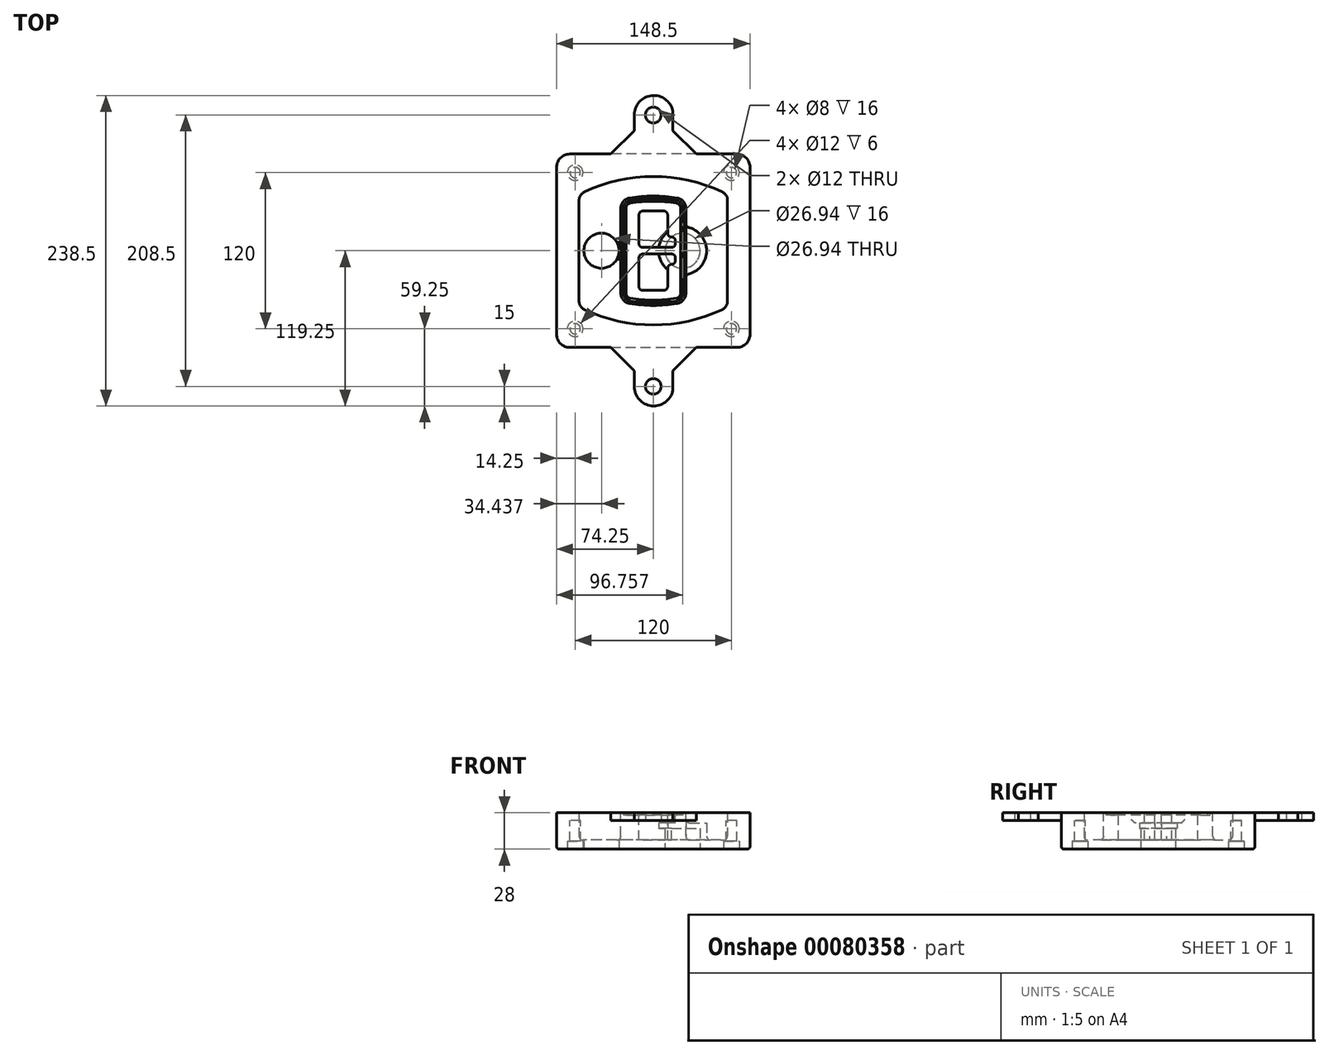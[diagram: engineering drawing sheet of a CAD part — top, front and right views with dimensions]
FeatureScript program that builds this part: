
annotation { "Feature Type Name" : "Feature", "Feature Type Description" : "" }
export const myFeature = defineFeature(function(context is Context, id is Id, definition is map)
    precondition{}
    {
        {
            var Q0;
            Q0=qCreatedBy(makeId("Top.planeOp"),FACE);
            var sketch = newSketch(context, id + "F0", { "sketchPlane" : qUnion([Q0])});
            skPoint(sketch, "E0.rect.middle", {"position": v(0, 0) * mm});
            skLineSegment(sketch, "E1.bottom", {"start": v(-64.25, -74.25) * mm, "end": v(64.25, -74.25) * mm});
            skLineSegment(sketch, "E1.top", {"start": v(-64.25, 74.25) * mm, "end": v(64.25, 74.25) * mm});
            skLineSegment(sketch, "E1.left", {"start": v(-74.25, -64.25) * mm, "end": v(-74.25, 64.25) * mm});
            skLineSegment(sketch, "E1.right", {"start": v(74.25, -64.25) * mm, "end": v(74.25, 64.25) * mm});
            skLineSegment(sketch, "E2", {"start": v(-74.25, 74.25) * mm, "end": v(74.25, -74.25) * mm, "construction": true});
            skLineSegment(sketch, "E3", {"start": v(74.25, 74.25) * mm, "end": v(-74.25, -74.25) * mm, "construction": true});
            skCircle(sketch, "E4", {"center": v(-60, 60) * mm, "radius": 4 * mm});
            skCircle(sketch, "E5", {"center": v(60, 60) * mm, "radius": 4 * mm});
            skCircle(sketch, "E6", {"center": v(60, -60) * mm, "radius": 4 * mm});
            skCircle(sketch, "E7", {"center": v(-60, -60) * mm, "radius": 4 * mm});
            skLineSegment(sketch, "E8", {"start": v(-60, 60) * mm, "end": v(60, 60) * mm, "construction": true});
            skLineSegment(sketch, "E9", {"start": v(60, 60) * mm, "end": v(60, -60) * mm, "construction": true});
            skLineSegment(sketch, "E10", {"start": v(60, -60) * mm, "end": v(-60, -60) * mm, "construction": true});
            skLineSegment(sketch, "E11", {"start": v(-60, -60) * mm, "end": v(-60, 60) * mm, "construction": true});
            skLineSegment(sketch, "E12", {"start": v(-60, 38.83) * mm, "end": v(-60, -38.83) * mm});
            skLineSegment(sketch, "E13", {"start": v(60, 38.83) * mm, "end": v(60, -38.83) * mm});
            skArc(sketch, "E14", {"start": v(54.26, 47.88) * mm, "mid": v(0, 60) * mm, "end": v(-54.26, 47.88) * mm});
            skArc(sketch, "E15", {"start": v(-54.26, -47.88) * mm, "mid": v(0, -60) * mm, "end": v(54.26, -47.88) * mm});
            skLineSegment(sketch, "E16", {"start": v(-60, 0) * mm, "end": v(60, 0) * mm, "construction": true});
            skPoint(sketch, "E17.visualSharp", {"position": v(-60, -45) * mm});
            skArc(sketch, "E17.filletArc", {"start": v(-60, -38.83) * mm, "mid": v(-58.44, -44.2) * mm, "end": v(-54.26, -47.88) * mm});
            skPoint(sketch, "E18.visualSharp", {"position": v(-60, 45) * mm});
            skArc(sketch, "E18.filletArc", {"start": v(-54.26, 47.88) * mm, "mid": v(-58.44, 44.2) * mm, "end": v(-60, 38.83) * mm});
            skPoint(sketch, "E19.visualSharp", {"position": v(60, 45) * mm});
            skArc(sketch, "E19.filletArc", {"start": v(60, 38.83) * mm, "mid": v(58.44, 44.2) * mm, "end": v(54.26, 47.88) * mm});
            skPoint(sketch, "E20.visualSharp", {"position": v(60, -45) * mm});
            skArc(sketch, "E20.filletArc", {"start": v(54.26, -47.88) * mm, "mid": v(58.44, -44.2) * mm, "end": v(60, -38.83) * mm});
            skPoint(sketch, "E21.visualSharp", {"position": v(-74.25, 74.25) * mm});
            skArc(sketch, "E21.filletArc", {"start": v(-64.25, 74.25) * mm, "mid": v(-71.32, 71.32) * mm, "end": v(-74.25, 64.25) * mm});
            skPoint(sketch, "E22.visualSharp", {"position": v(74.25, 74.25) * mm});
            skArc(sketch, "E22.filletArc", {"start": v(74.25, 64.25) * mm, "mid": v(71.32, 71.32) * mm, "end": v(64.25, 74.25) * mm});
            skPoint(sketch, "E23.visualSharp", {"position": v(74.25, -74.25) * mm});
            skArc(sketch, "E23.filletArc", {"start": v(64.25, -74.25) * mm, "mid": v(71.32, -71.32) * mm, "end": v(74.25, -64.25) * mm});
            skPoint(sketch, "E24.visualSharp", {"position": v(-74.25, -74.25) * mm});
            skArc(sketch, "E24.filletArc", {"start": v(-74.25, -64.25) * mm, "mid": v(-71.32, -71.32) * mm, "end": v(-64.25, -74.25) * mm});
            skArc(sketch, "E25.0", {"start": v(57, 38.83) * mm, "mid": v(55.9, 42.58) * mm, "end": v(52.98, 45.17) * mm});
            skLineSegment(sketch, "E25.1", {"start": v(57, 38.83) * mm, "end": v(57, -38.83) * mm});
            skArc(sketch, "E25.2", {"start": v(52.98, -45.17) * mm, "mid": v(55.9, -42.58) * mm, "end": v(57, -38.83) * mm});
            skArc(sketch, "E25.3", {"start": v(-52.98, -45.17) * mm, "mid": v(0, -57) * mm, "end": v(52.98, -45.17) * mm});
            skArc(sketch, "E25.4", {"start": v(-57, -38.83) * mm, "mid": v(-55.9, -42.58) * mm, "end": v(-52.98, -45.17) * mm});
            skArc(sketch, "E25.5", {"start": v(52.98, 45.17) * mm, "mid": v(0, 57) * mm, "end": v(-52.98, 45.17) * mm});
            skLineSegment(sketch, "E25.6", {"start": v(-57, 38.83) * mm, "end": v(-57, -38.83) * mm});
            skArc(sketch, "E25.7", {"start": v(-52.98, 45.17) * mm, "mid": v(-55.9, 42.58) * mm, "end": v(-57, 38.83) * mm});
            skArc(sketch, "E26.0", {"start": v(-55.96, 51.5) * mm, "mid": v(-61.82, 46.33) * mm, "end": v(-64, 38.83) * mm});
            skArc(sketch, "E26.1", {"start": v(55.96, 51.5) * mm, "mid": v(0, 64) * mm, "end": v(-55.96, 51.5) * mm});
            skArc(sketch, "E26.2", {"start": v(64, 38.83) * mm, "mid": v(61.82, 46.33) * mm, "end": v(55.96, 51.5) * mm});
            skLineSegment(sketch, "E26.3", {"start": v(64, 38.83) * mm, "end": v(64, -38.83) * mm});
            skArc(sketch, "E26.4", {"start": v(55.96, -51.5) * mm, "mid": v(61.82, -46.33) * mm, "end": v(64, -38.83) * mm});
            skLineSegment(sketch, "E26.5", {"start": v(-64, 38.83) * mm, "end": v(-64, -38.83) * mm});
            skArc(sketch, "E26.6", {"start": v(-55.96, -51.5) * mm, "mid": v(0, -64) * mm, "end": v(55.96, -51.5) * mm});
            skArc(sketch, "E26.7", {"start": v(-64, -38.83) * mm, "mid": v(-61.82, -46.33) * mm, "end": v(-55.96, -51.5) * mm});
            skSolve(sketch);
        }
        {
            var Q0;
            Q0=makeQuery(id+"F0.imprint","IMPRINT",FACE,{"disambiguationData":[TD([[makeQuery(id+"F0.imprint","IMPRINT",EDGE,{"derivedFrom":sQuery(id+"F0.wireOp",EDGE,"E1.bottom")}),1.0]])]});
            var Q1;
            Q1=makeQuery(id+"F0.imprint","IMPRINT",FACE,{"disambiguationData":[TD([[makeQuery(id+"F0.imprint","IMPRINT",EDGE,{"derivedFrom":sQuery(id+"F0.wireOp",EDGE,"E12")}),1.0]])]});
            var Q2;
            Q2=makeQuery(id+"F0.imprint","IMPRINT",FACE,{"disambiguationData":[TD([[makeQuery(id+"F0.imprint","IMPRINT",EDGE,{"derivedFrom":sQuery(id+"F0.wireOp",EDGE,"E25.0")}),1.0]])]});
            var Q3;
            Q3=makeQuery(id+"F0.imprint","IMPRINT",FACE,{"disambiguationData":[TD([[makeQuery(id+"F0.imprint","IMPRINT",EDGE,{"derivedFrom":sQuery(id+"F0.wireOp",EDGE,"E12")}),-1.0]])]});
            extrude(context, id + "F1", {"entities" : qUnion([Q0, Q1, Q2, Q3]), "oppositeDirection" : true, "depth" : 25 * mm});
        }
        {
            var Q0;
            Q0=makeQuery(id+"F0.imprint","IMPRINT",FACE,{"disambiguationData":[TD([[makeQuery(id+"F0.imprint","IMPRINT",EDGE,{"derivedFrom":sQuery(id+"F0.wireOp",EDGE,"E12")}),1.0]])]});
            extrude(context, id + "F2", {"entities" : qUnion([Q0]), "operationType" : NewBodyOperationType.ADD, "depth" : 3 * mm});
        }
        {
            var Q0;
            Q0=makeQuery(id+"F0.imprint","IMPRINT",FACE,{"disambiguationData":[TD([[makeQuery(id+"F0.imprint","IMPRINT",EDGE,{"derivedFrom":sQuery(id+"F0.wireOp",EDGE,"E25.0")}),1.0]])]});
            extrude(context, id + "F3", {"entities" : qUnion([Q0]), "operationType" : NewBodyOperationType.REMOVE, "oppositeDirection" : true, "depth" : 18 * mm});
        }
        {
            var Q0;
            Q0=makeQuery(id+"F2.opExtrude","CAP_FACE",FACE,{"disambiguationData":[OSD([sQuery(id+"F0.wireOp",EDGE,"E12"),sQuery(id+"F0.wireOp",EDGE,"E13"),sQuery(id+"F0.wireOp",EDGE,"E14"),sQuery(id+"F0.wireOp",EDGE,"E15"),sQuery(id+"F0.wireOp",EDGE,"E17.filletArc"),sQuery(id+"F0.wireOp",EDGE,"E18.filletArc"),sQuery(id+"F0.wireOp",EDGE,"E19.filletArc"),sQuery(id+"F0.wireOp",EDGE,"E20.filletArc"),sQuery(id+"F0.wireOp",EDGE,"E25.0"),sQuery(id+"F0.wireOp",EDGE,"E25.1"),sQuery(id+"F0.wireOp",EDGE,"E25.2"),sQuery(id+"F0.wireOp",EDGE,"E25.3"),sQuery(id+"F0.wireOp",EDGE,"E25.4"),sQuery(id+"F0.wireOp",EDGE,"E25.5"),sQuery(id+"F0.wireOp",EDGE,"E25.6"),sQuery(id+"F0.wireOp",EDGE,"E25.7")])],"isStart":false});
            var sketch = newSketch(context, id + "F4", { "sketchPlane" : qUnion([Q0])});
            skArc(sketch, "E27.0", {"start": v(-18.34, -40.45) * mm, "mid": v(0, -42) * mm, "end": v(18.34, -40.45) * mm});
            skArc(sketch, "E28.0", {"start": v(18.34, 40.45) * mm, "mid": v(0, 42) * mm, "end": v(-18.34, 40.45) * mm});
            skLineSegment(sketch, "E29", {"start": v(-25, 32.57) * mm, "end": v(-25, -32.57) * mm});
            skLineSegment(sketch, "E30", {"start": v(25, 32.57) * mm, "end": v(25, -32.57) * mm});
            skLineSegment(sketch, "E31", {"start": v(-25, 39.1) * mm, "end": v(25, 39.1) * mm, "construction": true});
            skLineSegment(sketch, "E32", {"start": v(-25, -39.1) * mm, "end": v(25, -39.1) * mm, "construction": true});
            skPoint(sketch, "E33.visualSharp", {"position": v(-25, 39.1) * mm});
            skArc(sketch, "E33.filletArc", {"start": v(-18.34, 40.45) * mm, "mid": v(-23.11, 37.73) * mm, "end": v(-25, 32.57) * mm});
            skPoint(sketch, "E34.visualSharp", {"position": v(25, 39.1) * mm});
            skArc(sketch, "E34.filletArc", {"start": v(25, 32.57) * mm, "mid": v(23.11, 37.73) * mm, "end": v(18.34, 40.45) * mm});
            skPoint(sketch, "E35.visualSharp", {"position": v(25, -39.1) * mm});
            skArc(sketch, "E35.filletArc", {"start": v(18.34, -40.45) * mm, "mid": v(23.11, -37.73) * mm, "end": v(25, -32.57) * mm});
            skPoint(sketch, "E36.visualSharp", {"position": v(-25, -39.1) * mm});
            skArc(sketch, "E36.filletArc", {"start": v(-25, -32.57) * mm, "mid": v(-23.11, -37.73) * mm, "end": v(-18.34, -40.45) * mm});
            skArc(sketch, "E37.0", {"start": v(52.98, 45.17) * mm, "mid": v(0, 57) * mm, "end": v(-52.98, 45.17) * mm});
            skArc(sketch, "E37.1", {"start": v(-52.98, 45.17) * mm, "mid": v(-55.9, 42.58) * mm, "end": v(-57, 38.83) * mm});
            skLineSegment(sketch, "E37.2", {"start": v(-57, 38.83) * mm, "end": v(-57, -38.83) * mm});
            skArc(sketch, "E37.3", {"start": v(-57, -38.83) * mm, "mid": v(-55.9, -42.58) * mm, "end": v(-52.98, -45.17) * mm});
            skArc(sketch, "E37.4", {"start": v(-52.98, -45.17) * mm, "mid": v(0, -57) * mm, "end": v(52.98, -45.17) * mm});
            skArc(sketch, "E37.5", {"start": v(52.98, -45.17) * mm, "mid": v(55.9, -42.58) * mm, "end": v(57, -38.83) * mm});
            skLineSegment(sketch, "E37.6", {"start": v(57, 38.83) * mm, "end": v(57, -38.83) * mm});
            skArc(sketch, "E37.7", {"start": v(57, 38.83) * mm, "mid": v(55.9, 42.58) * mm, "end": v(52.98, 45.17) * mm});
            skLineSegment(sketch, "E38.0", {"start": v(23, 32.57) * mm, "end": v(23, -32.57) * mm});
            skArc(sketch, "E38.1", {"start": v(18, -38.48) * mm, "mid": v(21.58, -36.44) * mm, "end": v(23, -32.57) * mm});
            skArc(sketch, "E38.2", {"start": v(-18, -38.48) * mm, "mid": v(0, -40) * mm, "end": v(18, -38.48) * mm});
            skArc(sketch, "E38.3", {"start": v(-23, -32.57) * mm, "mid": v(-21.58, -36.44) * mm, "end": v(-18, -38.48) * mm});
            skLineSegment(sketch, "E38.4", {"start": v(-23, 32.57) * mm, "end": v(-23, -32.57) * mm});
            skArc(sketch, "E38.5", {"start": v(23, 32.57) * mm, "mid": v(21.58, 36.44) * mm, "end": v(18, 38.48) * mm});
            skArc(sketch, "E38.6", {"start": v(-18, 38.48) * mm, "mid": v(-21.58, 36.44) * mm, "end": v(-23, 32.57) * mm});
            skArc(sketch, "E38.7", {"start": v(18, 38.48) * mm, "mid": v(0, 40) * mm, "end": v(-18, 38.48) * mm});
            skArc(sketch, "E39.0", {"start": v(21, 32.57) * mm, "mid": v(20.06, 35.15) * mm, "end": v(17.67, 36.5) * mm});
            skLineSegment(sketch, "E39.1", {"start": v(21, 32.57) * mm, "end": v(21, -32.57) * mm});
            skArc(sketch, "E39.2", {"start": v(17.67, -36.5) * mm, "mid": v(20.06, -35.15) * mm, "end": v(21, -32.57) * mm});
            skArc(sketch, "E39.3", {"start": v(-17.67, -36.5) * mm, "mid": v(0, -38) * mm, "end": v(17.67, -36.5) * mm});
            skArc(sketch, "E39.4", {"start": v(-21, -32.57) * mm, "mid": v(-20.06, -35.15) * mm, "end": v(-17.67, -36.5) * mm});
            skArc(sketch, "E39.5", {"start": v(17.67, 36.5) * mm, "mid": v(0, 38) * mm, "end": v(-17.67, 36.5) * mm});
            skLineSegment(sketch, "E39.6", {"start": v(-21, 32.57) * mm, "end": v(-21, -32.57) * mm});
            skArc(sketch, "E39.7", {"start": v(-17.67, 36.5) * mm, "mid": v(-20.06, 35.15) * mm, "end": v(-21, 32.57) * mm});
            skLineSegment(sketch, "E40", {"start": v(-25, 0) * mm, "end": v(25, 0) * mm, "construction": true});
            skLineSegment(sketch, "E41", {"start": v(-11, 5.5) * mm, "end": v(-11, 27.5) * mm});
            skLineSegment(sketch, "E42", {"start": v(-8, 30.5) * mm, "end": v(8, 30.5) * mm});
            skLineSegment(sketch, "E43", {"start": v(11, 27.5) * mm, "end": v(11, 13.5) * mm});
            skLineSegment(sketch, "E44", {"start": v(14, 10.5) * mm, "end": v(14, 10.5) * mm});
            skLineSegment(sketch, "E45", {"start": v(17, 7.5) * mm, "end": v(17, 5.5) * mm});
            skLineSegment(sketch, "E46", {"start": v(14, 2.5) * mm, "end": v(-8, 2.5) * mm});
            skPoint(sketch, "E47.visualSharp", {"position": v(-11, 30.5) * mm});
            skArc(sketch, "E47.filletArc", {"start": v(-8, 30.5) * mm, "mid": v(-10.12, 29.62) * mm, "end": v(-11, 27.5) * mm});
            skPoint(sketch, "E48.visualSharp", {"position": v(11, 30.5) * mm});
            skArc(sketch, "E48.filletArc", {"start": v(11, 27.5) * mm, "mid": v(10.12, 29.62) * mm, "end": v(8, 30.5) * mm});
            skPoint(sketch, "E49.visualSharp", {"position": v(11, 10.5) * mm});
            skArc(sketch, "E49.filletArc", {"start": v(11, 13.5) * mm, "mid": v(11.88, 11.38) * mm, "end": v(14, 10.5) * mm});
            skPoint(sketch, "E50.visualSharp", {"position": v(17, 10.5) * mm});
            skArc(sketch, "E50.filletArc", {"start": v(17, 7.5) * mm, "mid": v(16.12, 9.62) * mm, "end": v(14, 10.5) * mm});
            skPoint(sketch, "E51.visualSharp", {"position": v(17, 2.5) * mm});
            skArc(sketch, "E51.filletArc", {"start": v(14, 2.5) * mm, "mid": v(16.12, 3.38) * mm, "end": v(17, 5.5) * mm});
            skPoint(sketch, "E52.visualSharp", {"position": v(-11, 2.5) * mm});
            skArc(sketch, "E52.filletArc", {"start": v(-11, 5.5) * mm, "mid": v(-10.12, 3.38) * mm, "end": v(-8, 2.5) * mm});
            skLineSegment(sketch, "E53.0.MirrorCS", {"start": v(14, -2.5) * mm, "end": v(-8, -2.5) * mm});
            skArc(sketch, "E54.0.MirrorCS", {"start": v(-11, -5.5) * mm, "mid": v(-10.12, -3.38) * mm, "end": v(-8, -2.5) * mm});
            skLineSegment(sketch, "E55.0.MirrorCS", {"start": v(-11, -5.5) * mm, "end": v(-11, -27.5) * mm});
            skArc(sketch, "E56.0.MirrorCS", {"start": v(-8, -30.5) * mm, "mid": v(-10.12, -29.62) * mm, "end": v(-11, -27.5) * mm});
            skLineSegment(sketch, "E57.0.MirrorCS", {"start": v(-8, -30.5) * mm, "end": v(8, -30.5) * mm});
            skArc(sketch, "E58.0.MirrorCS", {"start": v(11, -27.5) * mm, "mid": v(10.12, -29.62) * mm, "end": v(8, -30.5) * mm});
            skLineSegment(sketch, "E59.0.MirrorCS", {"start": v(11, -27.5) * mm, "end": v(11, -13.5) * mm});
            skArc(sketch, "E60.0.MirrorCS", {"start": v(11, -13.5) * mm, "mid": v(11.88, -11.38) * mm, "end": v(14, -10.5) * mm});
            skArc(sketch, "E61.0.MirrorCS", {"start": v(17, -7.5) * mm, "mid": v(16.12, -9.62) * mm, "end": v(14, -10.5) * mm});
            skLineSegment(sketch, "E62.0.MirrorCS", {"start": v(17, -7.5) * mm, "end": v(17, -5.5) * mm});
            skArc(sketch, "E63.0.MirrorCS", {"start": v(14, -2.5) * mm, "mid": v(16.12, -3.38) * mm, "end": v(17, -5.5) * mm});
            skSolve(sketch);
        }
        {
            var Q0;
            Q0=makeQuery(id+"F4.imprint","IMPRINT",FACE,{"disambiguationData":[TD([[makeQuery(id+"F4.imprint","IMPRINT",EDGE,{"derivedFrom":sQuery(id+"F4.wireOp",EDGE,"E27.0")}),1.0]])]});
            var Q1;
            Q1=makeQuery(id+"F4.imprint","IMPRINT",FACE,{"disambiguationData":[TD([[makeQuery(id+"F4.imprint","IMPRINT",EDGE,{"derivedFrom":sQuery(id+"F4.wireOp",EDGE,"E38.0")}),-1.0]])]});
            var Q2;
            Q2=makeQuery(id+"F4.imprint","IMPRINT",FACE,{"disambiguationData":[TD([[makeQuery(id+"F4.imprint","IMPRINT",EDGE,{"derivedFrom":sQuery(id+"F4.wireOp",EDGE,"E39.0")}),1.0]])]});
            extrude(context, id + "F5", {"entities" : qUnion([Q0, Q1, Q2]), "operationType" : NewBodyOperationType.ADD, "endBound" : BoundingType.UP_TO_NEXT, "oppositeDirection" : true, "depth" : 25 * mm});
        }
        {
            var Q0;
            Q0=makeQuery(id+"F4.imprint","IMPRINT",FACE,{"disambiguationData":[TD([[makeQuery(id+"F4.imprint","IMPRINT",EDGE,{"derivedFrom":sQuery(id+"F4.wireOp",EDGE,"E38.0")}),-1.0]])]});
            extrude(context, id + "F6", {"entities" : qUnion([Q0]), "operationType" : NewBodyOperationType.REMOVE, "oppositeDirection" : true, "depth" : 2 * mm});
        }
        {
            var Q0;
            Q0=makeQuery(id+"F1.opExtrude","CAP_FACE",FACE,{"disambiguationData":[OSD([sQuery(id+"F0.wireOp",EDGE,"E1.bottom"),sQuery(id+"F0.wireOp",EDGE,"E1.top"),sQuery(id+"F0.wireOp",EDGE,"E1.left"),sQuery(id+"F0.wireOp",EDGE,"E1.right"),sQuery(id+"F0.wireOp",EDGE,"E4"),sQuery(id+"F0.wireOp",EDGE,"E5"),sQuery(id+"F0.wireOp",EDGE,"E6"),sQuery(id+"F0.wireOp",EDGE,"E7"),sQuery(id+"F0.wireOp",EDGE,"E21.filletArc"),sQuery(id+"F0.wireOp",EDGE,"E22.filletArc"),sQuery(id+"F0.wireOp",EDGE,"E23.filletArc"),sQuery(id+"F0.wireOp",EDGE,"E24.filletArc")])],"isStart":false});
            var sketch = newSketch(context, id + "F7", { "sketchPlane" : qUnion([Q0])});
            skCircle(sketch, "E64", {"center": v(22.5, 0) * mm, "radius": 13.47 * mm});
            skCircle(sketch, "E65", {"center": v(-39.81, 0) * mm, "radius": 13.47 * mm});
            skLineSegment(sketch, "E66", {"start": v(74.25, 0) * mm, "end": v(-74.25, 0) * mm});
            skCircle(sketch, "E67", {"center": v(22.5, 0) * mm, "radius": 18.47 * mm});
            skCircle(sketch, "E68", {"center": v(60, -60) * mm, "radius": 6 * mm});
            skCircle(sketch, "E69", {"center": v(-60, -60) * mm, "radius": 6 * mm});
            skCircle(sketch, "E70", {"center": v(-60, 60) * mm, "radius": 6 * mm});
            skCircle(sketch, "E71", {"center": v(60, 60) * mm, "radius": 6 * mm});
            skSolve(sketch);
        }
        {
            var Q0;
            {var subQ1=sQuery(id+"F7.wireOp",EDGE,"E66");var subQ4=sQuery(id+"F7.wireOp",EDGE,"E64");var subQ6=makeQuery(id+"F7.imprint","INTERSECT",VERTEX,{"disambiguationData":[OD(0.0)],"derivedFrom":[subQ4,subQ1]});Q0=makeQuery(id+"F7.imprint","IMPRINT",FACE,{"disambiguationData":[TD([[makeQuery(id+"F7.imprint","IMPRINT",EDGE,{"disambiguationData":[TD([[subQ6,-1.0]])],"derivedFrom":subQ4}),-1.0]])]});}
            var Q1;
            {var subQ0=sQuery(id+"F7.wireOp",EDGE,"E66");var subQ1=sQuery(id+"F7.wireOp",EDGE,"E64");var subQ3=makeQuery(id+"F7.imprint","INTERSECT",VERTEX,{"disambiguationData":[OD(0.0)],"derivedFrom":[subQ1,subQ0]});Q1=makeQuery(id+"F7.imprint","IMPRINT",FACE,{"disambiguationData":[TD([[makeQuery(id+"F7.imprint","IMPRINT",EDGE,{"disambiguationData":[TD([[subQ3,-1.0]])],"derivedFrom":subQ1}),1.0]])]});}
            var Q2;
            {var subQ0=sQuery(id+"F7.wireOp",EDGE,"E66");var subQ1=sQuery(id+"F7.wireOp",EDGE,"E64");var subQ3=makeQuery(id+"F7.imprint","INTERSECT",VERTEX,{"disambiguationData":[OD(0.0)],"derivedFrom":[subQ1,subQ0]});Q2=makeQuery(id+"F7.imprint","IMPRINT",FACE,{"disambiguationData":[TD([[makeQuery(id+"F7.imprint","IMPRINT",EDGE,{"disambiguationData":[TD([[subQ3,1.0]])],"derivedFrom":subQ1}),1.0]])]});}
            var Q3;
            {var subQ1=sQuery(id+"F7.wireOp",EDGE,"E66");var subQ4=sQuery(id+"F7.wireOp",EDGE,"E64");var subQ6=makeQuery(id+"F7.imprint","INTERSECT",VERTEX,{"disambiguationData":[OD(0.0)],"derivedFrom":[subQ4,subQ1]});Q3=makeQuery(id+"F7.imprint","IMPRINT",FACE,{"disambiguationData":[TD([[makeQuery(id+"F7.imprint","IMPRINT",EDGE,{"disambiguationData":[TD([[subQ6,1.0]])],"derivedFrom":subQ4}),-1.0]])]});}
            extrude(context, id + "F8", {"entities" : qUnion([Q0, Q1, Q2, Q3]), "operationType" : NewBodyOperationType.ADD, "oppositeDirection" : true, "depth" : 20 * mm});
        }
        {
            var Q0;
            {var subQ0=sQuery(id+"F7.wireOp",EDGE,"E66");var subQ1=sQuery(id+"F7.wireOp",EDGE,"E64");var subQ3=makeQuery(id+"F7.imprint","INTERSECT",VERTEX,{"disambiguationData":[OD(0.0)],"derivedFrom":[subQ1,subQ0]});Q0=makeQuery(id+"F7.imprint","IMPRINT",FACE,{"disambiguationData":[TD([[makeQuery(id+"F7.imprint","IMPRINT",EDGE,{"disambiguationData":[TD([[subQ3,-1.0]])],"derivedFrom":subQ1}),1.0]])]});}
            var Q1;
            {var subQ0=sQuery(id+"F7.wireOp",EDGE,"E66");var subQ1=sQuery(id+"F7.wireOp",EDGE,"E64");var subQ3=makeQuery(id+"F7.imprint","INTERSECT",VERTEX,{"disambiguationData":[OD(0.0)],"derivedFrom":[subQ1,subQ0]});Q1=makeQuery(id+"F7.imprint","IMPRINT",FACE,{"disambiguationData":[TD([[makeQuery(id+"F7.imprint","IMPRINT",EDGE,{"disambiguationData":[TD([[subQ3,1.0]])],"derivedFrom":subQ1}),1.0]])]});}
            extrude(context, id + "F9", {"entities" : qUnion([Q0, Q1]), "operationType" : NewBodyOperationType.REMOVE, "oppositeDirection" : true, "depth" : 16 * mm});
        }
        {
            var Q0;
            {var subQ0=sQuery(id+"F7.wireOp",EDGE,"E66");var subQ1=sQuery(id+"F7.wireOp",EDGE,"E65");var subQ3=makeQuery(id+"F7.imprint","INTERSECT",VERTEX,{"disambiguationData":[OD(0.0)],"derivedFrom":[subQ1,subQ0]});Q0=makeQuery(id+"F7.imprint","IMPRINT",FACE,{"disambiguationData":[TD([[makeQuery(id+"F7.imprint","IMPRINT",EDGE,{"disambiguationData":[TD([[subQ3,-1.0]])],"derivedFrom":subQ1}),1.0]])]});}
            var Q1;
            {var subQ0=sQuery(id+"F7.wireOp",EDGE,"E66");var subQ1=sQuery(id+"F7.wireOp",EDGE,"E65");var subQ3=makeQuery(id+"F7.imprint","INTERSECT",VERTEX,{"disambiguationData":[OD(0.0)],"derivedFrom":[subQ1,subQ0]});Q1=makeQuery(id+"F7.imprint","IMPRINT",FACE,{"disambiguationData":[TD([[makeQuery(id+"F7.imprint","IMPRINT",EDGE,{"disambiguationData":[TD([[subQ3,1.0]])],"derivedFrom":subQ1}),1.0]])]});}
            extrude(context, id + "F10", {"entities" : qUnion([Q0, Q1]), "operationType" : NewBodyOperationType.REMOVE, "oppositeDirection" : true, "depth" : 25 * mm});
        }
        {
            var Q0;
            Q0=makeQuery(id+"F7.imprint","IMPRINT",FACE,{"disambiguationData":[TD([[makeQuery(id+"F7.imprint","IMPRINT",EDGE,{"derivedFrom":sQuery(id+"F7.wireOp",EDGE,"E68")}),1.0]])]});
            var Q1;
            Q1=makeQuery(id+"F7.imprint","IMPRINT",FACE,{"disambiguationData":[TD([[makeQuery(id+"F7.imprint","IMPRINT",EDGE,{"derivedFrom":makeQuery(id+"F1.opExtrude","CAP_EDGE",EDGE,{"disambiguationData":[OSD([sQuery(id+"F0.wireOp",EDGE,"E5")])],"isStart":false})}),-1.0]])]});
            var Q2;
            Q2=makeQuery(id+"F7.imprint","IMPRINT",FACE,{"disambiguationData":[TD([[makeQuery(id+"F7.imprint","IMPRINT",EDGE,{"derivedFrom":sQuery(id+"F7.wireOp",EDGE,"E69")}),1.0]])]});
            var Q3;
            Q3=makeQuery(id+"F7.imprint","IMPRINT",FACE,{"disambiguationData":[TD([[makeQuery(id+"F7.imprint","IMPRINT",EDGE,{"derivedFrom":makeQuery(id+"F1.opExtrude","CAP_EDGE",EDGE,{"disambiguationData":[OSD([sQuery(id+"F0.wireOp",EDGE,"E4")])],"isStart":false})}),-1.0]])]});
            var Q4;
            Q4=makeQuery(id+"F7.imprint","IMPRINT",FACE,{"disambiguationData":[TD([[makeQuery(id+"F7.imprint","IMPRINT",EDGE,{"derivedFrom":sQuery(id+"F7.wireOp",EDGE,"E70")}),1.0]])]});
            var Q5;
            Q5=makeQuery(id+"F7.imprint","IMPRINT",FACE,{"disambiguationData":[TD([[makeQuery(id+"F7.imprint","IMPRINT",EDGE,{"derivedFrom":makeQuery(id+"F1.opExtrude","CAP_EDGE",EDGE,{"disambiguationData":[OSD([sQuery(id+"F0.wireOp",EDGE,"E7")])],"isStart":false})}),-1.0]])]});
            var Q6;
            Q6=makeQuery(id+"F7.imprint","IMPRINT",FACE,{"disambiguationData":[TD([[makeQuery(id+"F7.imprint","IMPRINT",EDGE,{"derivedFrom":sQuery(id+"F7.wireOp",EDGE,"E71")}),1.0]])]});
            var Q7;
            Q7=makeQuery(id+"F7.imprint","IMPRINT",FACE,{"disambiguationData":[TD([[makeQuery(id+"F7.imprint","IMPRINT",EDGE,{"derivedFrom":makeQuery(id+"F1.opExtrude","CAP_EDGE",EDGE,{"disambiguationData":[OSD([sQuery(id+"F0.wireOp",EDGE,"E6")])],"isStart":false})}),-1.0]])]});
            extrude(context, id + "F11", {"entities" : qUnion([Q0, Q1, Q2, Q3, Q4, Q5, Q6, Q7]), "operationType" : NewBodyOperationType.REMOVE, "oppositeDirection" : true, "depth" : 6 * mm});
        }
        {
            var Q0;
            Q0=makeQuery(id+"F9.boolean.opBoolean","COPY",FACE,{"derivedFrom":makeQuery(id+"F9.opExtrude","CAP_FACE",FACE,{"disambiguationData":[OSD([sQuery(id+"F7.wireOp",EDGE,"E64")])],"isStart":false})});
            var sketch = newSketch(context, id + "F12", { "sketchPlane" : qUnion([Q0])});
            skArc(sketch, "E72.0", {"start": v(11, 14.45) * mm, "mid": v(6.45, 9.13) * mm, "end": v(4.2, 2.5) * mm});
            skArc(sketch, "E72.1", {"start": v(4.2, -2.5) * mm, "mid": v(6.45, -9.13) * mm, "end": v(11, -14.45) * mm});
            skLineSegment(sketch, "E73", {"start": v(4.2, -2.5) * mm, "end": v(14, -2.5) * mm});
            skLineSegment(sketch, "E74.0", {"start": v(14, 2.5) * mm, "end": v(4.2, 2.5) * mm});
            skArc(sketch, "E74.1", {"start": v(14, 2.5) * mm, "mid": v(16.12, 3.38) * mm, "end": v(17, 5.5) * mm});
            skLineSegment(sketch, "E74.2", {"start": v(17, 7.5) * mm, "end": v(17, 5.5) * mm});
            skArc(sketch, "E74.3", {"start": v(17, 7.5) * mm, "mid": v(16.12, 9.62) * mm, "end": v(14, 10.5) * mm});
            skArc(sketch, "E74.4", {"start": v(11, 13.5) * mm, "mid": v(11.88, 11.38) * mm, "end": v(14, 10.5) * mm});
            skLineSegment(sketch, "E74.5", {"start": v(11, 14.45) * mm, "end": v(11, 13.5) * mm});
            skLineSegment(sketch, "E74.7", {"start": v(14, -2.5) * mm, "end": v(4.2, -2.5) * mm});
            skArc(sketch, "E74.8", {"start": v(14, -2.5) * mm, "mid": v(16.12, -3.38) * mm, "end": v(17, -5.5) * mm});
            skLineSegment(sketch, "E74.9", {"start": v(17, -7.5) * mm, "end": v(17, -5.5) * mm});
            skArc(sketch, "E74.10", {"start": v(17, -7.5) * mm, "mid": v(16.12, -9.62) * mm, "end": v(14, -10.5) * mm});
            skArc(sketch, "E74.11", {"start": v(11, -13.5) * mm, "mid": v(11.88, -11.38) * mm, "end": v(14, -10.5) * mm});
            skLineSegment(sketch, "E74.12", {"start": v(11, -14.45) * mm, "end": v(11, -13.5) * mm});
            skPoint(sketch, "E75.orphan", {"position": v(11, -27.5) * mm});
            skPoint(sketch, "E76.orphan", {"position": v(-8, -2.5) * mm});
            skPoint(sketch, "E77.orphan", {"position": v(-8, 2.5) * mm});
            skPoint(sketch, "E78.orphan", {"position": v(11, 27.5) * mm});
            skSolve(sketch);
        }
        {
            var Q0;
            {var subQ7=sQuery(id+"F12.wireOp",EDGE,"E72.0");var subQ14=sQuery(id+"F12.wireOp",EDGE,"E72.1");var subQ16=sQuery(id+"F12.wireOp",EDGE,"E74.1");var subQ18=sQuery(id+"F12.wireOp",EDGE,"E74.8");Q0=qUnion([makeQuery(id+"F12.imprint","IMPRINT",FACE,{"disambiguationData":[TD([[makeQuery(id+"F12.imprint","IMPRINT",EDGE,{"derivedFrom":subQ7}),1.0]])]}),makeQuery(id+"F12.imprint","IMPRINT",FACE,{"disambiguationData":[TD([[makeQuery(id+"F12.imprint","IMPRINT",EDGE,{"derivedFrom":subQ14}),1.0]])]}),makeQuery(id+"F12.imprint","IMPRINT",FACE,{"disambiguationData":[TD([[makeQuery(id+"F12.imprint","IMPRINT",EDGE,{"derivedFrom":subQ16}),1.0]])]}),makeQuery(id+"F12.imprint","IMPRINT",FACE,{"disambiguationData":[TD([[makeQuery(id+"F12.imprint","IMPRINT",EDGE,{"derivedFrom":subQ18}),-1.0]])]})]);}
            var Q1;
            Q1=makeQuery(id+"F5.boolean.opBoolean","SPLIT",FACE,{"disambiguationData":[TD([makeQuery(id+"F5.opExtrude","SWEPT_FACE",FACE,{"disambiguationData":[OSD([sQuery(id+"F4.wireOp",EDGE,"E41")])]})])],"derivedFrom":makeQuery(id+"F3.boolean.opBoolean","COPY",FACE,{"derivedFrom":makeQuery(id+"F3.opExtrude","CAP_FACE",FACE,{"disambiguationData":[OSD([sQuery(id+"F0.wireOp",EDGE,"E25.0"),sQuery(id+"F0.wireOp",EDGE,"E25.1"),sQuery(id+"F0.wireOp",EDGE,"E25.2"),sQuery(id+"F0.wireOp",EDGE,"E25.3"),sQuery(id+"F0.wireOp",EDGE,"E25.4"),sQuery(id+"F0.wireOp",EDGE,"E25.5"),sQuery(id+"F0.wireOp",EDGE,"E25.6"),sQuery(id+"F0.wireOp",EDGE,"E25.7")])],"isStart":false})})});
            extrude(context, id + "F13", {"entities" : qUnion([Q0]), "operationType" : NewBodyOperationType.REMOVE, "endBound" : BoundingType.UP_TO_SURFACE, "endBoundEntityFace" : qUnion([Q1]), "depth" : 25 * mm});
        }
        {
            var Q0;
            Q0=makeQuery(id+"F3.boolean.opBoolean","COPY",EDGE,{"derivedFrom":makeQuery(id+"F3.opExtrude","CAP_EDGE",EDGE,{"disambiguationData":[OSD([sQuery(id+"F0.wireOp",EDGE,"E25.6")])],"isStart":false})});
            var Q1;
            Q1=makeQuery(id+"F8.boolean.opBoolean","INTERSECT",EDGE,{"derivedFrom":[makeQuery(id+"F5.opExtrude","SWEPT_FACE",FACE,{"disambiguationData":[OSD([sQuery(id+"F4.wireOp",EDGE,"E30")])]}),makeQuery(id+"F8.opExtrude","CAP_FACE",FACE,{"disambiguationData":[OSD([sQuery(id+"F7.wireOp",EDGE,"E67")])],"isStart":false})]});
            var Q2;
            Q2=makeQuery(id+"F8.boolean.opBoolean","INTERSECT",EDGE,{"disambiguationData":[OD(1.0)],"derivedFrom":[makeQuery(id+"F5.opExtrude","SWEPT_FACE",FACE,{"disambiguationData":[OSD([sQuery(id+"F4.wireOp",EDGE,"E30")])]}),makeQuery(id+"F8.opExtrude","SWEPT_FACE",FACE,{"disambiguationData":[OSD([sQuery(id+"F7.wireOp",EDGE,"E67")])]})]});
            var Q3;
            {var subQ0=sQuery(id+"F4.wireOp",EDGE,"E30");Q3=makeQuery(id+"F8.boolean.opBoolean","SPLIT",EDGE,{"disambiguationData":[TD([makeQuery(id+"F5.opExtrude","SWEPT_FACE",FACE,{"disambiguationData":[OSD([sQuery(id+"F4.wireOp",EDGE,"E35.filletArc")])]})])],"derivedFrom":makeQuery(id+"F5.opExtrude","CAP_EDGE",EDGE,{"disambiguationData":[OSD([subQ0])],"isStart":false})});}
            var Q4;
            {var subQ0=sQuery(id+"F0.wireOp",EDGE,"E25.7");var subQ1=sQuery(id+"F0.wireOp",EDGE,"E25.1");var subQ2=sQuery(id+"F0.wireOp",EDGE,"E25.6");var subQ3=sQuery(id+"F0.wireOp",EDGE,"E25.5");var subQ4=sQuery(id+"F0.wireOp",EDGE,"E25.4");var subQ5=sQuery(id+"F0.wireOp",EDGE,"E25.0");var subQ6=sQuery(id+"F0.wireOp",EDGE,"E25.2");var subQ7=sQuery(id+"F0.wireOp",EDGE,"E25.3");Q4=makeQuery(id+"F8.boolean.opBoolean","INTERSECT",EDGE,{"derivedFrom":[makeQuery(id+"F5.boolean.opBoolean","SPLIT",FACE,{"disambiguationData":[TD([makeQuery(id+"F2.opExtrude","SWEPT_FACE",FACE,{"disambiguationData":[OSD([subQ5])]})])],"derivedFrom":makeQuery(id+"F3.boolean.opBoolean","COPY",FACE,{"derivedFrom":makeQuery(id+"F3.opExtrude","CAP_FACE",FACE,{"disambiguationData":[OSD([subQ5,subQ1,subQ6,subQ7,subQ4,subQ3,subQ2,subQ0])],"isStart":false})})}),makeQuery(id+"F8.opExtrude","SWEPT_FACE",FACE,{"disambiguationData":[OSD([sQuery(id+"F7.wireOp",EDGE,"E67")])]})]});}
            var Q5;
            Q5=makeQuery(id+"F8.boolean.opBoolean","INTERSECT",EDGE,{"disambiguationData":[OD(0.0)],"derivedFrom":[makeQuery(id+"F5.opExtrude","SWEPT_FACE",FACE,{"disambiguationData":[OSD([sQuery(id+"F4.wireOp",EDGE,"E30")])]}),makeQuery(id+"F8.opExtrude","SWEPT_FACE",FACE,{"disambiguationData":[OSD([sQuery(id+"F7.wireOp",EDGE,"E67")])]})]});
            fillet(context, id + "F14", {"entities" : qUnion([Q0, Q1, Q2, Q3, Q4, Q5]), "radius" : 3 * mm, "tangentPropagation" : true, "allowEdgeOverflow" : false});
        }
        {
            var Q0;
            Q0=makeQuery(id+"F1.opExtrude","CAP_EDGE",EDGE,{"disambiguationData":[OSD([sQuery(id+"F0.wireOp",EDGE,"E1.bottom")])],"isStart":false});
            fillet(context, id + "F15", {"entities" : qUnion([Q0]), "radius" : 2 * mm, "tangentPropagation" : true, "allowEdgeOverflow" : false});
        }
        {
            var Q0;
            {var subQ0=sQuery(id+"F0.wireOp",EDGE,"E22.filletArc");var subQ1=sQuery(id+"F0.wireOp",EDGE,"E7");var subQ2=sQuery(id+"F0.wireOp",EDGE,"E6");var subQ3=sQuery(id+"F0.wireOp",EDGE,"E5");var subQ4=sQuery(id+"F0.wireOp",EDGE,"E4");var subQ5=sQuery(id+"F0.wireOp",EDGE,"E1.bottom");var subQ6=sQuery(id+"F0.wireOp",EDGE,"E21.filletArc");var subQ7=sQuery(id+"F0.wireOp",EDGE,"E1.top");var subQ8=sQuery(id+"F0.wireOp",EDGE,"E1.left");var subQ9=sQuery(id+"F0.wireOp",EDGE,"E1.right");var subQ10=sQuery(id+"F0.wireOp",EDGE,"E23.filletArc");var subQ11=sQuery(id+"F0.wireOp",EDGE,"E24.filletArc");Q0=makeQuery(id+"F2.boolean.opBoolean","SPLIT",FACE,{"disambiguationData":[TD([makeQuery(id+"F1.opExtrude","SWEPT_FACE",FACE,{"disambiguationData":[OSD([subQ5])]})])],"derivedFrom":makeQuery(id+"F1.opExtrude","CAP_FACE",FACE,{"disambiguationData":[OSD([subQ5,subQ7,subQ8,subQ9,subQ4,subQ3,subQ2,subQ1,subQ6,subQ0,subQ10,subQ11])],"isStart":true})});}
            var sketch = newSketch(context, id + "F16", { "sketchPlane" : qUnion([Q0])});
            skLineSegment(sketch, "E79.0", {"start": v(-64.25, 74.25) * mm, "end": v(64.25, 74.25) * mm});
            skArc(sketch, "E79.1", {"start": v(-64.25, 74.25) * mm, "mid": v(-71.32, 71.32) * mm, "end": v(-74.25, 64.25) * mm});
            skLineSegment(sketch, "E79.2", {"start": v(-74.25, -64.25) * mm, "end": v(-74.25, 64.25) * mm});
            skArc(sketch, "E79.3", {"start": v(-74.25, -64.25) * mm, "mid": v(-71.32, -71.32) * mm, "end": v(-64.25, -74.25) * mm});
            skArc(sketch, "E79.5", {"start": v(64.25, -74.25) * mm, "mid": v(71.32, -71.32) * mm, "end": v(74.25, -64.25) * mm});
            skLineSegment(sketch, "E79.6", {"start": v(74.25, -64.25) * mm, "end": v(74.25, 64.25) * mm});
            skArc(sketch, "E79.7", {"start": v(74.25, 64.25) * mm, "mid": v(71.32, 71.32) * mm, "end": v(64.25, 74.25) * mm});
            skCircle(sketch, "E79.8", {"center": v(60, 60) * mm, "radius": 4 * mm});
            skCircle(sketch, "E79.9", {"center": v(-60, 60) * mm, "radius": 4 * mm});
            skCircle(sketch, "E79.10", {"center": v(-60, -60) * mm, "radius": 4 * mm});
            skCircle(sketch, "E79.11", {"center": v(60, -60) * mm, "radius": 4 * mm});
            skLineSegment(sketch, "E80", {"start": v(33, 74.25) * mm, "end": v(15, 92.25) * mm});
            skLineSegment(sketch, "E81", {"start": v(15, 92.25) * mm, "end": v(15, 107.29) * mm});
            skCircle(sketch, "E82", {"center": v(0, 104.25) * mm, "radius": 6 * mm});
            skLineSegment(sketch, "E83", {"start": v(0, 104.25) * mm, "end": v(0, 74.25) * mm, "construction": true});
            skLineSegment(sketch, "E84", {"start": v(0, 0) * mm, "end": v(109.8, 0) * mm, "construction": true});
            skPoint(sketch, "E84.endSnap0", {"position": v(74.25, 0) * mm});
            skLineSegment(sketch, "E85", {"start": v(109.8, 0) * mm, "end": v(0, 0) * mm, "construction": true});
            skLineSegment(sketch, "E86", {"start": v(0, 0) * mm, "end": v(-107.56, 0) * mm, "construction": true});
            skLineSegment(sketch, "E87", {"start": v(-107.56, 0) * mm, "end": v(0, 0) * mm, "construction": true});
            skLineSegment(sketch, "E88", {"start": v(0, 104.25) * mm, "end": v(-36.7, 104.25) * mm, "construction": true});
            skLineSegment(sketch, "E89", {"start": v(0, 104.25) * mm, "end": v(48.73, 104.25) * mm, "construction": true});
            skLineSegment(sketch, "E90", {"start": v(-32.69, 74.25) * mm, "end": v(-14.69, 92.25) * mm});
            skLineSegment(sketch, "E91", {"start": v(-14.69, 92.25) * mm, "end": v(-14.69, 104.25) * mm});
            skArc(sketch, "E92", {"start": v(15, 107.29) * mm, "mid": v(-1.22, 119.17) * mm, "end": v(-14.69, 104.25) * mm});
            skLineSegment(sketch, "E93.MirrorCS", {"start": v(-32.69, -74.25) * mm, "end": v(-14.69, -92.25) * mm});
            skLineSegment(sketch, "E94.MirrorCS", {"start": v(-14.69, -92.25) * mm, "end": v(-14.69, -104.25) * mm});
            skArc(sketch, "E95.MirrorCS", {"start": v(15, -107.29) * mm, "mid": v(-1.22, -119.17) * mm, "end": v(-14.69, -104.25) * mm});
            skLineSegment(sketch, "E96.MirrorCS", {"start": v(15, -92.25) * mm, "end": v(15, -107.29) * mm});
            skLineSegment(sketch, "E97.MirrorCS", {"start": v(33, -74.25) * mm, "end": v(15, -92.25) * mm});
            skCircle(sketch, "E98.MirrorC", {"center": v(0, -104.25) * mm, "radius": 6 * mm});
            skSolve(sketch);
        }
        {
            var Q0;
            Q0=makeQuery(id+"F16.imprint","IMPRINT",FACE,{"disambiguationData":[TD([[makeQuery(id+"F16.imprint","IMPRINT",EDGE,{"derivedFrom":sQuery(id+"F16.wireOp",EDGE,"E79.8")}),1.0]])]});
            var Q1;
            Q1=makeQuery(id+"F16.imprint","IMPRINT",FACE,{"disambiguationData":[TD([[makeQuery(id+"F16.imprint","IMPRINT",EDGE,{"derivedFrom":sQuery(id+"F16.wireOp",EDGE,"E79.9")}),1.0]])]});
            var Q2;
            Q2=makeQuery(id+"F16.imprint","IMPRINT",FACE,{"disambiguationData":[TD([[makeQuery(id+"F16.imprint","IMPRINT",EDGE,{"derivedFrom":sQuery(id+"F16.wireOp",EDGE,"E79.10")}),1.0]])]});
            var Q3;
            Q3=makeQuery(id+"F16.imprint","IMPRINT",FACE,{"disambiguationData":[TD([[makeQuery(id+"F16.imprint","IMPRINT",EDGE,{"derivedFrom":sQuery(id+"F16.wireOp",EDGE,"E79.11")}),1.0]])]});
            var Q4;
            {var subQ0=sQuery(id+"F16.wireOp",EDGE,"E80");Q4=makeQuery(id+"F16.imprint","IMPRINT",FACE,{"disambiguationData":[TD([[makeQuery(id+"F16.imprint","IMPRINT",EDGE,{"derivedFrom":subQ0}),1.0]])]});}
            var Q5;
            {var subQ0=sQuery(id+"F16.wireOp",EDGE,"E79.1");Q5=makeQuery(id+"F16.imprint","IMPRINT",FACE,{"disambiguationData":[TD([[makeQuery(id+"F16.imprint","IMPRINT",EDGE,{"derivedFrom":subQ0}),1.0]])]});}
            var Q6;
            {var subQ0=sQuery(id+"F16.wireOp",EDGE,"E93.MirrorCS");Q6=makeQuery(id+"F16.imprint","IMPRINT",FACE,{"disambiguationData":[TD([[makeQuery(id+"F16.imprint","IMPRINT",EDGE,{"derivedFrom":subQ0}),1.0]])]});}
            extrude(context, id + "F17", {"entities" : qUnion([Q0, Q1, Q2, Q3, Q4, Q5, Q6]), "operationType" : NewBodyOperationType.ADD, "endBound" : BoundingType.SYMMETRIC, "depth" : 6 * mm});
        }
    });
